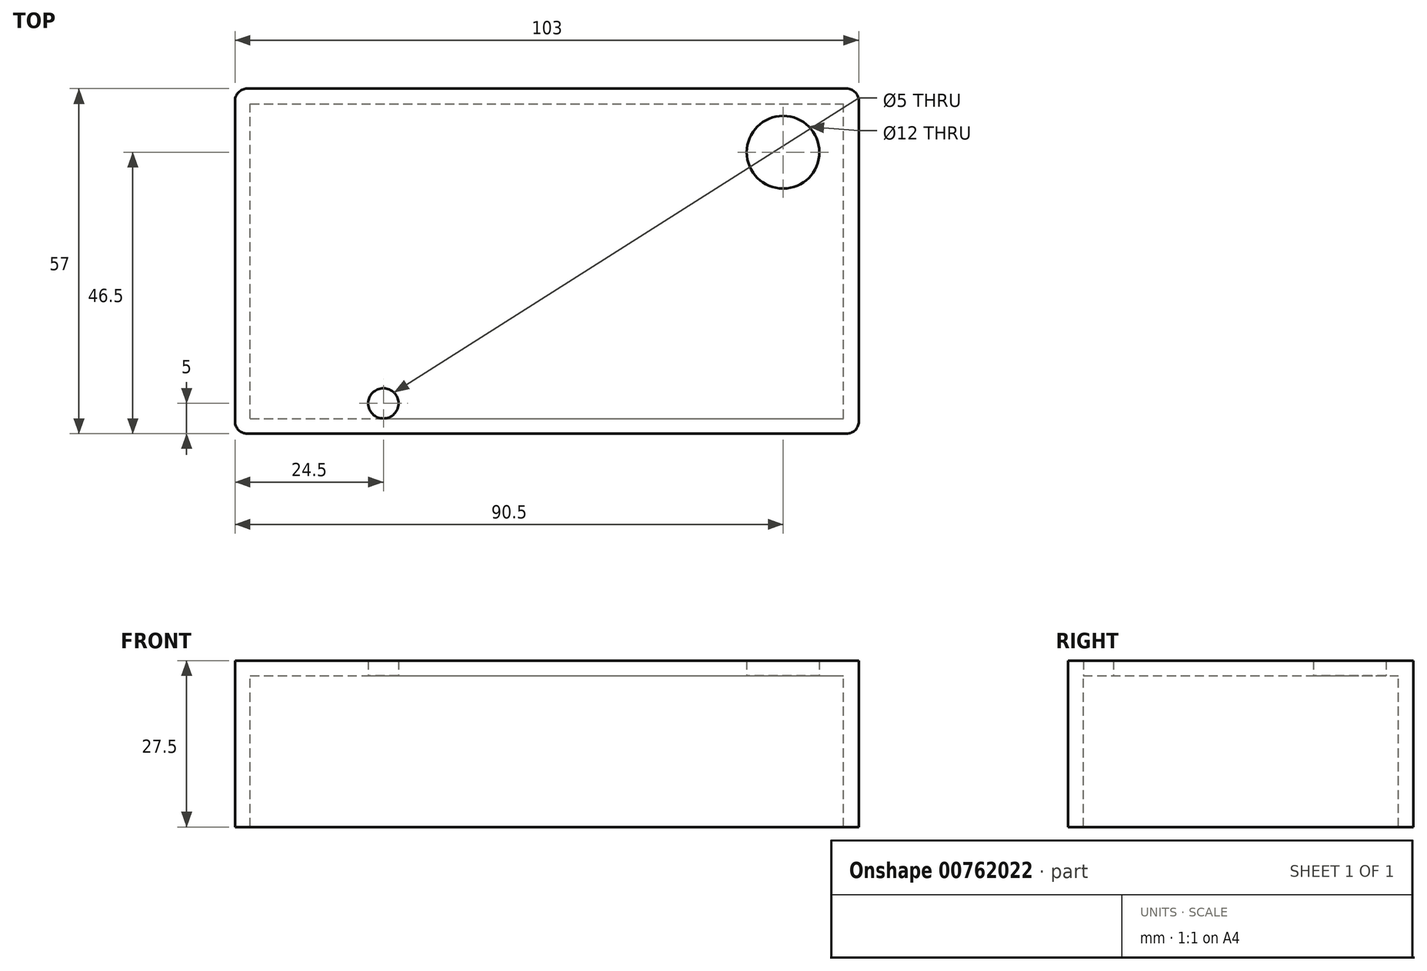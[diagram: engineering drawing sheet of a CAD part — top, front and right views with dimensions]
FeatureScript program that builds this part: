
annotation { "Feature Type Name" : "Feature", "Feature Type Description" : "" }
export const myFeature = defineFeature(function(context is Context, id is Id, definition is map)
    precondition{}
    {
        {
            var Q0;
            Q0=qCreatedBy(makeId("Top.planeOp"),FACE);
            var sketch = newSketch(context, id + "F0", { "sketchPlane" : qUnion([Q0])});
            skLineSegment(sketch, "E0.bottom", {"start": v(0, 0) * mm, "end": v(98, 0) * mm});
            skLineSegment(sketch, "E0.top", {"start": v(0, 52) * mm, "end": v(98, 52) * mm});
            skLineSegment(sketch, "E0.left", {"start": v(0, 0) * mm, "end": v(0, 52) * mm});
            skLineSegment(sketch, "E0.right", {"start": v(98, 0) * mm, "end": v(98, 52) * mm});
            skCircle(sketch, "E1", {"center": v(22, 2.5) * mm, "radius": 2.5 * mm});
            skCircle(sketch, "E2", {"center": v(88, 44) * mm, "radius": 6 * mm});
            skLineSegment(sketch, "E3.0", {"start": v(-0.5, 54.5) * mm, "end": v(98.5, 54.5) * mm});
            skLineSegment(sketch, "E3.1", {"start": v(-2.5, -0.5) * mm, "end": v(-2.5, 52.5) * mm});
            skLineSegment(sketch, "E3.2", {"start": v(-0.5, -2.5) * mm, "end": v(98.5, -2.5) * mm});
            skLineSegment(sketch, "E3.3", {"start": v(100.5, -0.5) * mm, "end": v(100.5, 52.5) * mm});
            skPoint(sketch, "E4.visualSharp", {"position": v(100.5, 54.5) * mm});
            skArc(sketch, "E4.filletArc", {"start": v(100.5, 52.5) * mm, "mid": v(99.91, 53.91) * mm, "end": v(98.5, 54.5) * mm});
            skPoint(sketch, "E5.visualSharp", {"position": v(100.5, -2.5) * mm});
            skArc(sketch, "E5.filletArc", {"start": v(98.5, -2.5) * mm, "mid": v(99.91, -1.91) * mm, "end": v(100.5, -0.5) * mm});
            skPoint(sketch, "E6.visualSharp", {"position": v(-2.5, -2.5) * mm});
            skArc(sketch, "E6.filletArc", {"start": v(-2.5, -0.5) * mm, "mid": v(-1.91, -1.91) * mm, "end": v(-0.5, -2.5) * mm});
            skPoint(sketch, "E7.visualSharp", {"position": v(-2.5, 54.5) * mm});
            skArc(sketch, "E7.filletArc", {"start": v(-0.5, 54.5) * mm, "mid": v(-1.91, 53.91) * mm, "end": v(-2.5, 52.5) * mm});
            skSolve(sketch);
        }
        {
            var Q0;
            Q0 = qSketchRegion(id + "F0", true);
            var Q1;
            Q1=makeQuery(id+"F0.imprint","IMPRINT",FACE,{"disambiguationData":[TD([[makeQuery(id+"F0.imprint","IMPRINT",EDGE,{"derivedFrom":sQuery(id+"F0.wireOp",EDGE,"E0.top")}),-1.0]])]});
            extrude(context, id + "F1", {"entities" : qUnion([Q0, Q1]), "depth" : 2.5 * mm, "offsetDistance" : 25 * mm});
        }
        {
            var Q0;
            Q0=qCreatedBy(makeId("Top.planeOp"),FACE);
            var sketch = newSketch(context, id + "F2", { "sketchPlane" : qUnion([Q0])});
            skLineSegment(sketch, "E8.bottom", {"start": v(0, 0) * mm, "end": v(98, 0) * mm});
            skLineSegment(sketch, "E8.top", {"start": v(0, 52) * mm, "end": v(98, 52) * mm});
            skLineSegment(sketch, "E8.left", {"start": v(0, 0) * mm, "end": v(0, 52) * mm});
            skLineSegment(sketch, "E8.right", {"start": v(98, 0) * mm, "end": v(98, 52) * mm});
            skLineSegment(sketch, "E9.0", {"start": v(-0.5, 54.5) * mm, "end": v(98.5, 54.5) * mm});
            skLineSegment(sketch, "E9.1", {"start": v(-2.5, -0.5) * mm, "end": v(-2.5, 52.5) * mm});
            skLineSegment(sketch, "E9.2", {"start": v(-0.5, -2.5) * mm, "end": v(98.5, -2.5) * mm});
            skLineSegment(sketch, "E9.3", {"start": v(100.5, -0.5) * mm, "end": v(100.5, 52.5) * mm});
            skPoint(sketch, "E10.visualSharp", {"position": v(100.5, 54.5) * mm});
            skArc(sketch, "E10.filletArc", {"start": v(100.5, 52.5) * mm, "mid": v(99.91, 53.91) * mm, "end": v(98.5, 54.5) * mm});
            skPoint(sketch, "E11.visualSharp", {"position": v(100.5, -2.5) * mm});
            skArc(sketch, "E11.filletArc", {"start": v(98.5, -2.5) * mm, "mid": v(99.91, -1.91) * mm, "end": v(100.5, -0.5) * mm});
            skPoint(sketch, "E12.visualSharp", {"position": v(-2.5, -2.5) * mm});
            skArc(sketch, "E12.filletArc", {"start": v(-2.5, -0.5) * mm, "mid": v(-1.91, -1.91) * mm, "end": v(-0.5, -2.5) * mm});
            skPoint(sketch, "E13.visualSharp", {"position": v(-2.5, 54.5) * mm});
            skArc(sketch, "E13.filletArc", {"start": v(-0.5, 54.5) * mm, "mid": v(-1.91, 53.91) * mm, "end": v(-2.5, 52.5) * mm});
            skSolve(sketch);
        }
        {
            var Q0;
            Q0 = qSketchRegion(id + "F2", true);
            extrude(context, id + "F3", {"entities" : qUnion([Q0]), "operationType" : NewBodyOperationType.ADD, "oppositeDirection" : true, "depth" : 25 * mm, "offsetDistance" : 25 * mm});
        }
    });
